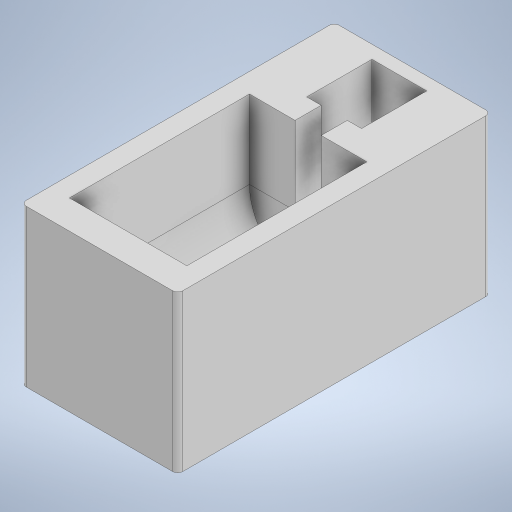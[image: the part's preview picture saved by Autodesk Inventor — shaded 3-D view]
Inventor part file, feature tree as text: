
AUTODESK INVENTOR PART (.ipt)
format: ipt  version: 2023 (Build 270158000, 158)  size: 718,336 bytes
history: native  units: in
note: dims shown in document units (in); Inventor stores cm internally (conversion verified against a paired STEP export)
features: extrude x8, plane x7, sketch x6, fillet x3, chamfer x2, projected_geometry x2
ambient origin geometry x8: Origin, YZ Plane, XZ Plane, XY Plane, X Axis, Y Axis, Z Axis, Center Point
bodies: Solid1 (feature_tree)
feature tree (28):
  sketch  "Sketch1"  dims[d0=2.3622in d1=4.7244in d2=1.7717in d3=0.1969in d4=0.9843in d5=0.0394in d6=0.4921in d7=0.3937in d8=0.0984in d9=0.8858in d10=-2.7165in d11=0.9843in d12=90.0deg d13=0.8268in d14=0.1969in d15=0.3937in d16=90.0deg d17=0.3937in d18=-2.7165in d19=90.0deg d20=-1.3583in d21=1.7717in d22=2.3622in d23=0.0in]
  extrude  "Extrusion1"  Depth=2.3622in TaperAngle=0.0deg
  sketch  "Sketch2"  dims[d24=-0.1969in d25=0.8268in]
  plane  "Work Plane1"
  plane  "Work Plane2"
  plane  "Work Plane3"
  plane  "Work Plane5"
  sketch  "Sketch3"  dims[d28=0.3937in d29=0.0in d30=0.3937in]
  plane  "Work Plane6"
  extrude  "Extrusion3"  Depth=0.8268in
  sketch  "Sketch4"  dims[d31=1.7717in d32=0.3937in d33=0.0in]
  sketch  "Sketch5"  dims[d34=0.3937in d35=0.0in d36=0.3937in d37=0.0in]
  extrude  "Extrusion4"  Depth=0.3937in
  plane  "Work Plane7"
  extrude  "Extrusion5"  Depth=0.3937in TaperAngle=0.0deg
  extrude  "Extrusion6"  Depth=0.3937in TaperAngle=0.0deg
  extrude  "Extrusion7"  Depth=0.3937in TaperAngle=0.0deg
  fillet  "Fillet1"  Radius=0.0787in
  extrude  "Extrusion8"  Depth=0.3937in
  chamfer  "Chamfer1"  Distance=0.3937in
  chamfer  "Chamfer2"  [1 undecoded]
  fillet  "Fillet2"  Radius=0.0787in
  fillet  "Fillet3"  Radius=0.0787in
  extrude  "Extrusion10"  Depth=0.0394in
  projected_geometry  "Projected Loop1"
  plane  "Work Plane4"
  sketch  "Sketch6"  dims[d38=-0.0787in d39=0.3937in d40=0.0in d41=0.0787in d42=0.3937in d43=0.3937in d44=0.0in d45=0.0in d46=0.0787in d47=0.0787in d48=45.0deg d49=0.0787in d50=0.0787in d51=45.0deg d52=0.0394in d53=0.0394in d58=0.2953in d59=0.7874in d61=1.1811in d62=0.7874in d64=1.1811in d67=0.1969in d68=0.0in]
  projected_geometry  "Projected Loop2"
note: 1 required parameter value undecoded (feature->parameter linkage not recoverable at this tier; creation-order binding heuristic only, values carry confidence <= 0.55)
